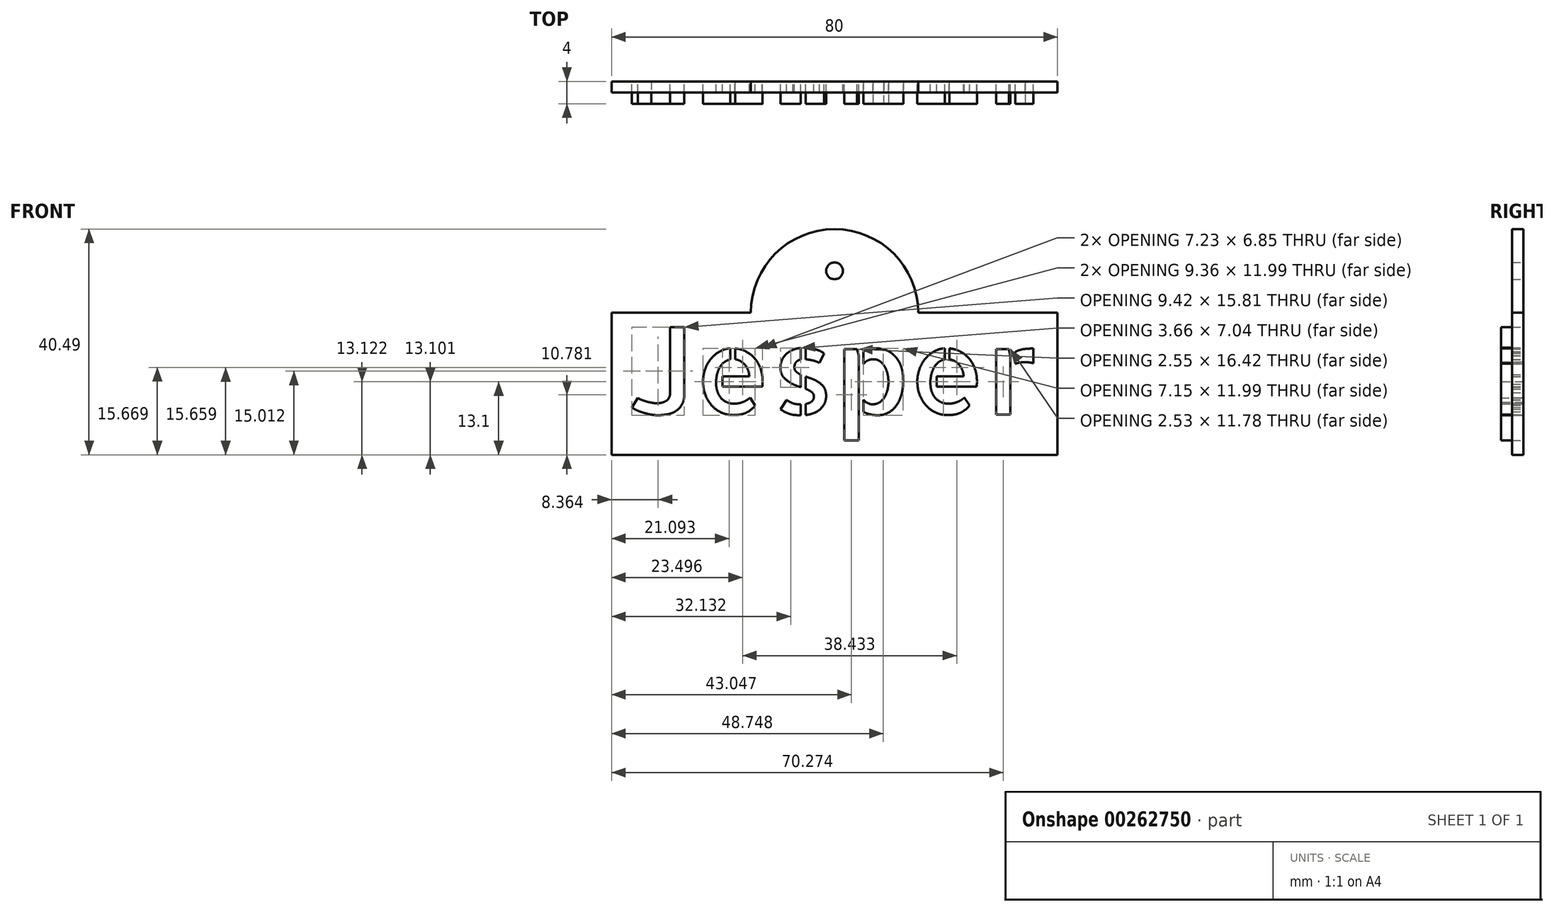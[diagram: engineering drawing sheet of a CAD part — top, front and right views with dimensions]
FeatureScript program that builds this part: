
annotation { "Feature Type Name" : "Feature", "Feature Type Description" : "" }
export const myFeature = defineFeature(function(context is Context, id is Id, definition is map)
    precondition{}
    {
        {
            var Q0;
            Q0=qCreatedBy(makeId("Front.planeOp"),FACE);
            var sketch = newSketch(context, id + "F0", { "sketchPlane" : qUnion([Q0])});
            skLineSegment(sketch, "E0.bottom", {"start": v(46.2, 8.65) * mm, "end": v(-33.8, 8.65) * mm});
            skLineSegment(sketch, "E0.top", {"start": v(46.2, 34.14) * mm, "end": v(21.2, 34.14) * mm});
            skLineSegment(sketch, "E0.left", {"start": v(46.2, 8.65) * mm, "end": v(46.2, 34.14) * mm});
            skLineSegment(sketch, "E0.right", {"start": v(-33.8, 8.65) * mm, "end": v(-33.8, 34.14) * mm});
            skPoint(sketch, "E0.middle", {"position": v(6.2, 21.4) * mm});
            skArc(sketch, "E1", {"start": v(21.2, 34.14) * mm, "mid": v(6.2, 49.14) * mm, "end": v(-8.8, 34.14) * mm});
            skPoint(sketch, "E2", {"position": v(-8.8, 34.14) * mm});
            skPoint(sketch, "E3", {"position": v(21.2, 34.14) * mm});
            skLineSegment(sketch, "E4.trimOffspring", {"start": v(-8.8, 34.14) * mm, "end": v(-33.8, 34.14) * mm});
            skCircle(sketch, "E5", {"center": v(6.2, 41.66) * mm, "radius": 1.5 * mm});
            skPoint(sketch, "E6.positionSnap0", {"position": v(6.2, 49.14) * mm});
            skText(sketch, "E7", { "text": "Jesper", "fontName": "AllertaStencil-Regular.ttf"});
            const initialGuessF0  = {"E7": [-0.0307, 0.01586, 1, 0, 0.0154]};
            skSetInitialGuess(sketch, initialGuessF0);
            skSolve(sketch);
        }
        {
            var Q0;
            Q0=makeQuery(id+"F0.imprint","IMPRINT",FACE,{"disambiguationData":[TD([[makeQuery(id+"F0.imprint","IMPRINT",EDGE,{"derivedFrom":sQuery(id+"F0.wireOp",EDGE,"E7.sketch_text.stroke-55")}),-1.0]])]});
            var Q1;
            Q1=makeQuery(id+"F0.imprint","IMPRINT",FACE,{"disambiguationData":[TD([[makeQuery(id+"F0.imprint","IMPRINT",EDGE,{"derivedFrom":sQuery(id+"F0.wireOp",EDGE,"E7.sketch_text.stroke-84")}),-1.0]])]});
            var Q2;
            Q2=makeQuery(id+"F0.imprint","IMPRINT",FACE,{"disambiguationData":[TD([[makeQuery(id+"F0.imprint","IMPRINT",EDGE,{"derivedFrom":sQuery(id+"F0.wireOp",EDGE,"E7.sketch_text.stroke-69")}),-1.0]])]});
            var Q3;
            Q3=makeQuery(id+"F0.imprint","IMPRINT",FACE,{"disambiguationData":[TD([[makeQuery(id+"F0.imprint","IMPRINT",EDGE,{"derivedFrom":sQuery(id+"F0.wireOp",EDGE,"E7.sketch_text.stroke-75")}),-1.0]])]});
            var Q4;
            {var subQ5=sQuery(id+"F0.wireOp",EDGE,"E7.sketch_text.stroke-98");Q4=makeQuery(id+"F0.imprint","IMPRINT",FACE,{"disambiguationData":[TD([[makeQuery(id+"F0.imprint","IMPRINT",EDGE,{"derivedFrom":subQ5}),-1.0]])]});}
            var Q5;
            Q5=makeQuery(id+"F0.imprint","IMPRINT",FACE,{"disambiguationData":[TD([[makeQuery(id+"F0.imprint","IMPRINT",EDGE,{"derivedFrom":sQuery(id+"F0.wireOp",EDGE,"E7.sketch_text.stroke-103")}),-1.0]])]});
            var Q6;
            Q6=makeQuery(id+"F0.imprint","IMPRINT",FACE,{"disambiguationData":[TD([[makeQuery(id+"F0.imprint","IMPRINT",EDGE,{"derivedFrom":sQuery(id+"F0.wireOp",EDGE,"E7.sketch_text.stroke-142")}),-1.0]])]});
            var Q7;
            Q7=makeQuery(id+"F0.imprint","IMPRINT",FACE,{"disambiguationData":[TD([[makeQuery(id+"F0.imprint","IMPRINT",EDGE,{"derivedFrom":sQuery(id+"F0.wireOp",EDGE,"E7.sketch_text.stroke-129")}),-1.0]])]});
            var Q8;
            Q8=makeQuery(id+"F0.imprint","IMPRINT",FACE,{"disambiguationData":[TD([[makeQuery(id+"F0.imprint","IMPRINT",EDGE,{"derivedFrom":sQuery(id+"F0.wireOp",EDGE,"E7.sketch_text.stroke-166")}),-1.0]])]});
            var Q9;
            Q9=makeQuery(id+"F0.imprint","IMPRINT",FACE,{"disambiguationData":[TD([[makeQuery(id+"F0.imprint","IMPRINT",EDGE,{"derivedFrom":sQuery(id+"F0.wireOp",EDGE,"E7.sketch_text.stroke-173")}),-1.0]])]});
            var Q10;
            Q10=makeQuery(id+"F0.imprint","IMPRINT",FACE,{"disambiguationData":[TD([[makeQuery(id+"F0.imprint","IMPRINT",EDGE,{"derivedFrom":sQuery(id+"F0.wireOp",EDGE,"E7.sketch_text.stroke-18")}),-1.0]])]});
            var Q11;
            Q11=makeQuery(id+"F0.imprint","IMPRINT",FACE,{"disambiguationData":[TD([[makeQuery(id+"F0.imprint","IMPRINT",EDGE,{"derivedFrom":sQuery(id+"F0.wireOp",EDGE,"E7.sketch_text.stroke-31")}),-1.0]])]});
            var Q12;
            Q12=makeQuery(id+"F0.imprint","IMPRINT",FACE,{"disambiguationData":[TD([[makeQuery(id+"F0.imprint","IMPRINT",EDGE,{"derivedFrom":sQuery(id+"F0.wireOp",EDGE,"E7.sketch_text.stroke-0")}),-1.0]])]});
            extrude(context, id + "F1", {"entities" : qUnion([Q0, Q1, Q2, Q3, Q4, Q5, Q6, Q7, Q8, Q9, Q10, Q11, Q12]), "depth" : 4 * mm});
        }
        {
            var Q0;
            Q0=makeQuery(id+"F0.imprint","IMPRINT",FACE,{"disambiguationData":[TD([[makeQuery(id+"F0.imprint","IMPRINT",EDGE,{"derivedFrom":sQuery(id+"F0.wireOp",EDGE,"E0.top")}),1.0]])]});
            extrude(context, id + "F2", {"entities" : qUnion([Q0]), "depth" : 2 * mm});
        }
    });
